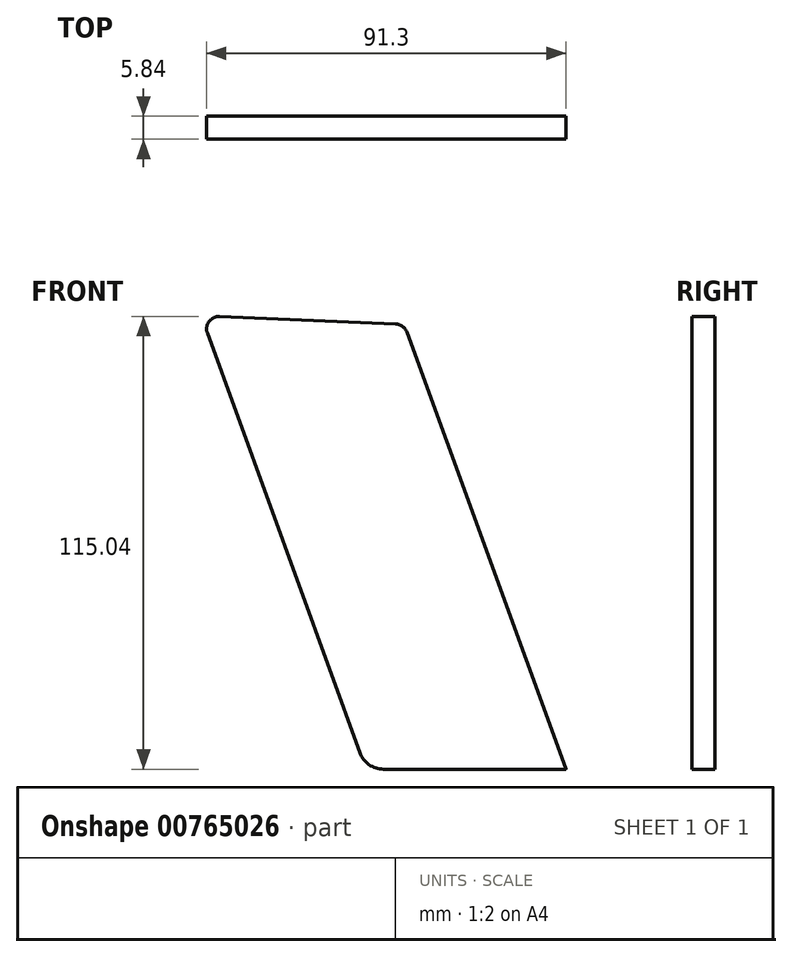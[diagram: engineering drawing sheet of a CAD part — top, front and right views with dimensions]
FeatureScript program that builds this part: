
annotation { "Feature Type Name" : "Feature", "Feature Type Description" : "" }
export const myFeature = defineFeature(function(context is Context, id is Id, definition is map)
    precondition{}
    {
        {
            var Q0;
            Q0=qCreatedBy(makeId("Front.planeOp"),FACE);
            var sketch = newSketch(context, id + "F0", { "sketchPlane" : qUnion([Q0])});
            skLineSegment(sketch, "E0", {"start": v(0, 0) * mm, "end": v(50.8, 0) * mm});
            skLineSegment(sketch, "E1", {"start": v(50.8, 0) * mm, "end": v(106.27, -152.4) * mm});
            skLineSegment(sketch, "E2", {"start": v(106.27, -152.4) * mm, "end": v(55.47, -152.4) * mm});
            skLineSegment(sketch, "E3", {"start": v(55.47, -152.4) * mm, "end": v(0, 0) * mm});
            skSolve(sketch);
        }
        {
            var Q0;
            Q0=qSketchRegion(id+"F0",true);
            extrude(context, id + "F1", {"entities" : qUnion([Q0]), "depth" : 5.84 * mm, "offsetDistance" : 25.4 * mm});
        }
        {
            var Q0;
            Q0=makeQuery(id+"F1.opExtrude","SWEPT_EDGE",EDGE,{"disambiguationData":[OSD([sQuery(id+"F0.wireOp",EDGE,"E2"),sQuery(id+"F0.wireOp",EDGE,"E3")])]});
            var Q1;
            Q1=makeQuery(id+"F1.opExtrude","SWEPT_EDGE",EDGE,{"disambiguationData":[OSD([sQuery(id+"F0.wireOp",EDGE,"E0"),sQuery(id+"F0.wireOp",EDGE,"E1")])]});
            var Q2;
            Q2=makeQuery(id+"F1.opExtrude","SWEPT_EDGE",EDGE,{"disambiguationData":[OSD([sQuery(id+"F0.wireOp",EDGE,"E0"),sQuery(id+"F0.wireOp",EDGE,"E3")])]});
            fillet(context, id + "F2", {"entities" : qUnion([Q0, Q1, Q2]), "radius" : 6.35 * mm, "tangentPropagation" : true, "allowEdgeOverflow" : false});
        }
        {
            var Q0;
            Q0=makeQuery(id+"F1.opExtrude","SWEPT_EDGE",EDGE,{"disambiguationData":[OSD([sQuery(id+"F0.wireOp",EDGE,"E1"),sQuery(id+"F0.wireOp",EDGE,"E2")])]});
            fillet(context, id + "F3", {"entities" : qUnion([Q0]), "radius" : 1 / 50.8 * mm, "tangentPropagation" : true, "allowEdgeOverflow" : false});
        }
        {
            var Q0;
            Q0=makeQuery(id+"F1.opExtrude","CAP_FACE",FACE,{"disambiguationData":[OSD([sQuery(id+"F0.wireOp",EDGE,"E0"),sQuery(id+"F0.wireOp",EDGE,"E1"),sQuery(id+"F0.wireOp",EDGE,"E2"),sQuery(id+"F0.wireOp",EDGE,"E3")])],"isStart":false});
            var sketch = newSketch(context, id + "F4", { "sketchPlane" : qUnion([Q0])});
            skLineSegment(sketch, "E4", {"start": v(9.07, 0) * mm, "end": v(64.54, -152.4) * mm, "construction": true});
            skLineSegment(sketch, "E5", {"start": v(64.54, -152.4) * mm, "end": v(172.86, -112.97) * mm, "construction": true});
            skSolve(sketch);
        }
        {
            var Q0;
            {var subQ0=sQuery(id+"F0.wireOp",EDGE,"E0");Q0=makeQuery(id+"F4.imprint","IMPRINT",FACE,{"disambiguationData":[TD([[makeQuery(id+"F4.imprint","IMPRINT",EDGE,{"derivedFrom":makeQuery(id+"F1.opExtrude","CAP_EDGE",EDGE,{"disambiguationData":[OSD([subQ0])],"isStart":false})}),-1.0]])]});}
            var sketch = newSketch(context, id + "F5", { "sketchPlane" : qUnion([Q0])});
            skLineSegment(sketch, "E6.bottom", {"start": v(-38.81, 0) * mm, "end": v(109.9, 0) * mm});
            skLineSegment(sketch, "E6.left", {"start": v(-38.81, 0) * mm, "end": v(-38.81, -34.93) * mm});
            skLineSegment(sketch, "E6.right", {"start": v(109.9, 0) * mm, "end": v(109.9, -41.28) * mm});
            skLineSegment(sketch, "E7", {"start": v(109.9, -41.28) * mm, "end": v(-38.81, -34.93) * mm});
            skPoint(sketch, "E8.orphan", {"position": v(-38.81, -41.28) * mm});
            skSolve(sketch);
        }
        {
            var Q0;
            Q0 = qSketchRegion(id + "F5", true);
            extrude(context, id + "F6", {"entities" : qUnion([Q0]), "operationType" : NewBodyOperationType.REMOVE, "oppositeDirection" : true, "depth" : 25.4 * mm, "offsetDistance" : 25.4 * mm});
        }
        {
            var Q0;
            Q0=makeQuery(id+"F6.boolean.opBoolean","INTERSECT",EDGE,{"derivedFrom":[makeQuery(id+"F1.opExtrude","SWEPT_FACE",FACE,{"disambiguationData":[OSD([sQuery(id+"F0.wireOp",EDGE,"E1")])]}),makeQuery(id+"F6.opExtrude","SWEPT_FACE",FACE,{"disambiguationData":[OSD([sQuery(id+"F5.wireOp",EDGE,"E7")])]})]});
            var Q1;
            Q1=makeQuery(id+"F6.boolean.opBoolean","INTERSECT",EDGE,{"derivedFrom":[makeQuery(id+"F1.opExtrude","SWEPT_FACE",FACE,{"disambiguationData":[OSD([sQuery(id+"F0.wireOp",EDGE,"E3")])]}),makeQuery(id+"F6.opExtrude","SWEPT_FACE",FACE,{"disambiguationData":[OSD([sQuery(id+"F5.wireOp",EDGE,"E7")])]})]});
            fillet(context, id + "F7", {"entities" : qUnion([Q0, Q1]), "radius" : 3.17 * mm, "tangentPropagation" : true, "allowEdgeOverflow" : false});
        }
    });
